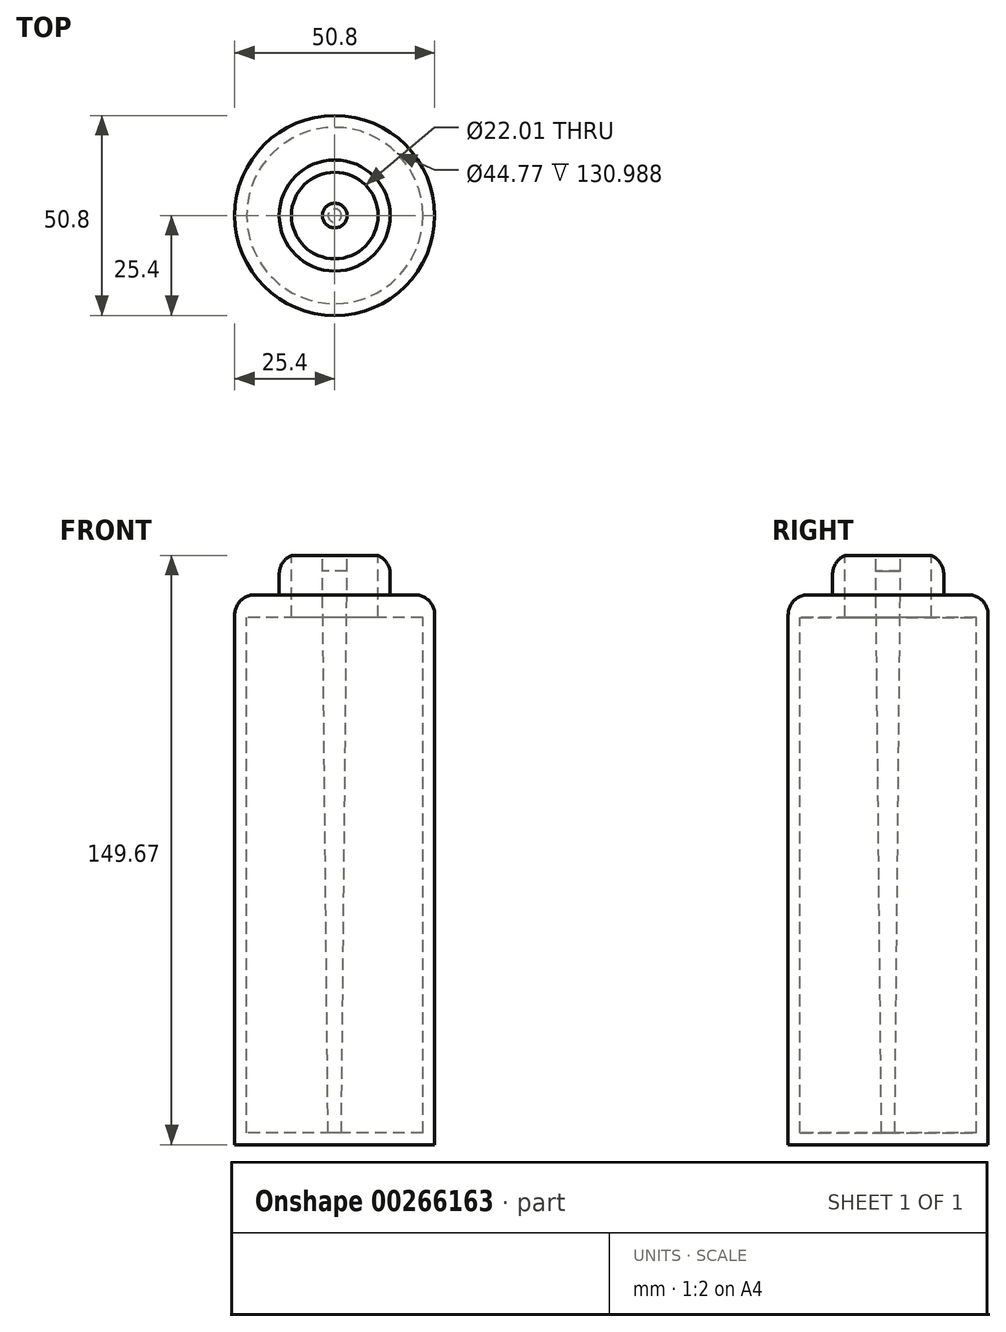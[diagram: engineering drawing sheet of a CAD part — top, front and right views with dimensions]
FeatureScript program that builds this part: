
annotation { "Feature Type Name" : "Feature", "Feature Type Description" : "" }
export const myFeature = defineFeature(function(context is Context, id is Id, definition is map)
    precondition{}
    {
        {
            var Q0;
            Q0=qCreatedBy(makeId("Front.planeOp"),FACE);
            var sketch = newSketch(context, id + "F0", { "sketchPlane" : qUnion([Q0])});
            skLineSegment(sketch, "E0.left", {"start": v(25.4, 69.85) * mm, "end": v(25.4, -69.85) * mm});
            skPoint(sketch, "E0.middle", {"position": v(0, 0) * mm});
            skLineSegment(sketch, "E1", {"start": v(14.1, 79.82) * mm, "end": v(14.1, 69.85) * mm});
            skLineSegment(sketch, "E2", {"start": v(14.1, 69.85) * mm, "end": v(25.4, 69.85) * mm});
            skLineSegment(sketch, "E3", {"start": v(0, 79.82) * mm, "end": v(0, 0) * mm});
            skLineSegment(sketch, "E4", {"start": v(25.4, -69.85) * mm, "end": v(0, -69.85) * mm});
            skLineSegment(sketch, "E5", {"start": v(0, -69.85) * mm, "end": v(0, 0) * mm});
            skLineSegment(sketch, "E6", {"start": v(11, 75.9) * mm, "end": v(11, 64.1) * mm});
            skLineSegment(sketch, "E7", {"start": v(11, 64.1) * mm, "end": v(22.39, 64.1) * mm});
            skLineSegment(sketch, "E8", {"start": v(22.39, 64.1) * mm, "end": v(22.39, -66.9) * mm});
            skLineSegment(sketch, "E9", {"start": v(22.39, -66.9) * mm, "end": v(1.7, -66.9) * mm});
            skLineSegment(sketch, "E10", {"start": v(1.7, -66.9) * mm, "end": v(3.14, 75.9) * mm});
            skLineSegment(sketch, "E11", {"start": v(11, 75.9) * mm, "end": v(11, 79.82) * mm});
            skLineSegment(sketch, "E12", {"start": v(3.14, 79.82) * mm, "end": v(3.14, 75.9) * mm});
            skLineSegment(sketch, "E13", {"start": v(3.14, 79.82) * mm, "end": v(0, 79.82) * mm});
            skLineSegment(sketch, "E14", {"start": v(14.1, 79.82) * mm, "end": v(11, 79.82) * mm});
            skSolve(sketch);
        }
        {
            var Q0;
            Q0=makeQuery(id+"F0.imprint","IMPRINT",FACE,{"disambiguationData":[TD([[makeQuery(id+"F0.imprint","IMPRINT",EDGE,{"derivedFrom":sQuery(id+"F0.wireOp",EDGE,"E0.left")}),-1.0]])]});
            var Q1;
            Q1=sQuery(id+"F0.wireOp",EDGE,"E3");
            revolve(context, id + "F1", {"entities" : qUnion([Q0]), "axis" : qUnion([Q1]), "revolveType" : RevolveType.FULL});
        }
        {
            var Q0;
            Q0=makeQuery(id+"F1.opRevolve","SWEPT_EDGE",EDGE,{"disambiguationData":[OSD([sQuery(id+"F0.wireOp",EDGE,"E0.left"),sQuery(id+"F0.wireOp",EDGE,"E2")])]});
            var Q1;
            Q1=makeQuery(id+"F1.opRevolve","SWEPT_EDGE",EDGE,{"disambiguationData":[OSD([sQuery(id+"F0.wireOp",EDGE,"E1"),sQuery(id+"F0.wireOp",EDGE,"E14")])]});
            fillet(context, id + "F2", {"entities" : qUnion([Q0, Q1]), "radius" : 5.08 * mm, "tangentPropagation" : true, "allowEdgeOverflow" : false});
        }
    });
